# Revit family: OP 71-20
name_source: partatom
category: Modelli generici
revit_build: Autodesk Revit 2017 (Build: 20160217_0900(x64)
units: mm (PartAtom-declared; Revit-internal decimal feet)

## family parameters
Basato su piano di lavoro = No
Condiviso = No
Punto di calcolo locali = No
Può ospitare armatura = No
Quota connettore circolare = Usa diametro
Sempre verticale = Sì
Taglio con vuoti quando caricato = No
Tipo di parte = Normale

## types (1)
- Standard
    Extrusion_End_1 = 0 mm  [stored 0 ft]
    Extrusion_End_2 = 0 mm  [stored 0 ft]
    Extrusion_End_3 = 0 mm  [stored 0 ft]
    Extrusion_End_4 = 0 mm  [stored 0 ft]
    d2 = 1990 mm  [stored 6.52887 ft]
    d258 = 0 mm  [stored 0 ft]
    d42 = 0 mm  [stored 0 ft]
    d93 = 0 mm  [stored 0 ft]
    d97 = 0 mm  [stored 0 ft]
    d99 = 0 mm  [stored 0 ft]

note: [stored X ft] marks values corroborated as IEEE doubles in the binary element streams (Revit-internal decimal feet)

## geometry (parser evidence)
native form markers: Extrusion x4
no freeform markers — native parametric forms only
